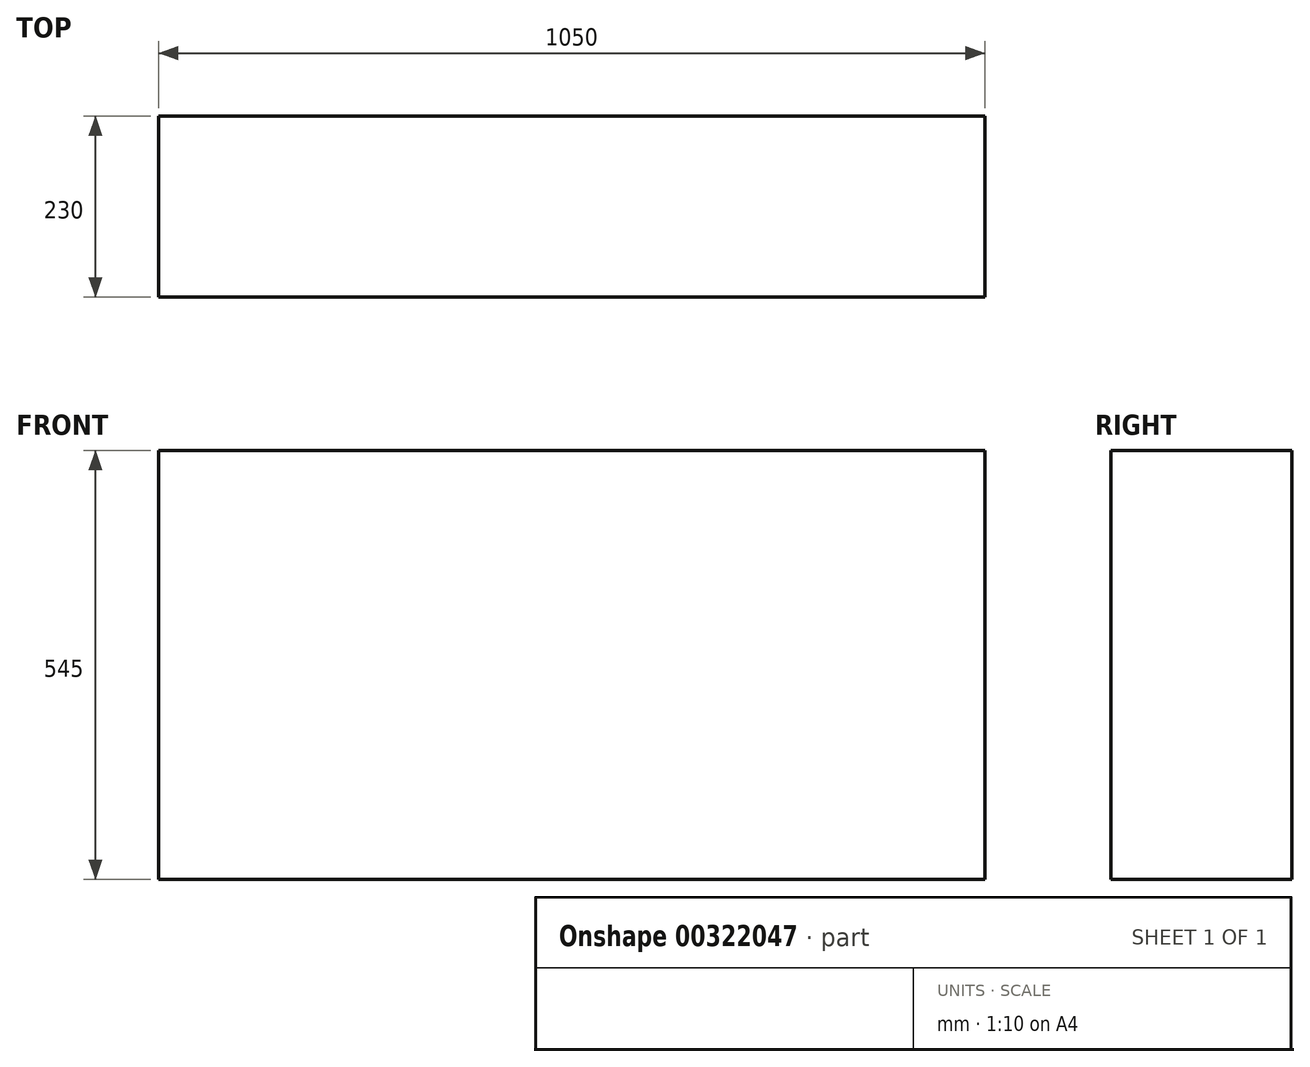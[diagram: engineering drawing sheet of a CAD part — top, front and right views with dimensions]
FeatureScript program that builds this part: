
annotation { "Feature Type Name" : "Feature", "Feature Type Description" : "" }
export const myFeature = defineFeature(function(context is Context, id is Id, definition is map)
    precondition{}
    {
        {
            var Q0;
            Q0=qCreatedBy(makeId("Front.planeOp"),FACE);
            var sketch = newSketch(context, id + "F0", { "sketchPlane" : qUnion([Q0])});
            skLineSegment(sketch, "E0.bottom", {"start": v(525, 272.5) * mm, "end": v(-525, 272.5) * mm});
            skLineSegment(sketch, "E0.top", {"start": v(525, -272.5) * mm, "end": v(-525, -272.5) * mm});
            skLineSegment(sketch, "E0.left", {"start": v(525, 272.5) * mm, "end": v(525, -272.5) * mm});
            skLineSegment(sketch, "E0.right", {"start": v(-525, 272.5) * mm, "end": v(-525, -272.5) * mm});
            skPoint(sketch, "E0.middle", {"position": v(0, 0) * mm});
            skSolve(sketch);
        }
        {
            var Q0;
            Q0=makeQuery(id+"F0.imprint","IMPRINT",FACE,{"disambiguationData":[TD([[makeQuery(id+"F0.imprint","IMPRINT",EDGE,{"derivedFrom":sQuery(id+"F0.wireOp",EDGE,"E0.bottom")}),1.0]])]});
            extrude(context, id + "F1", {"entities" : qUnion([Q0]), "depth" : 230 * mm});
        }
    });
